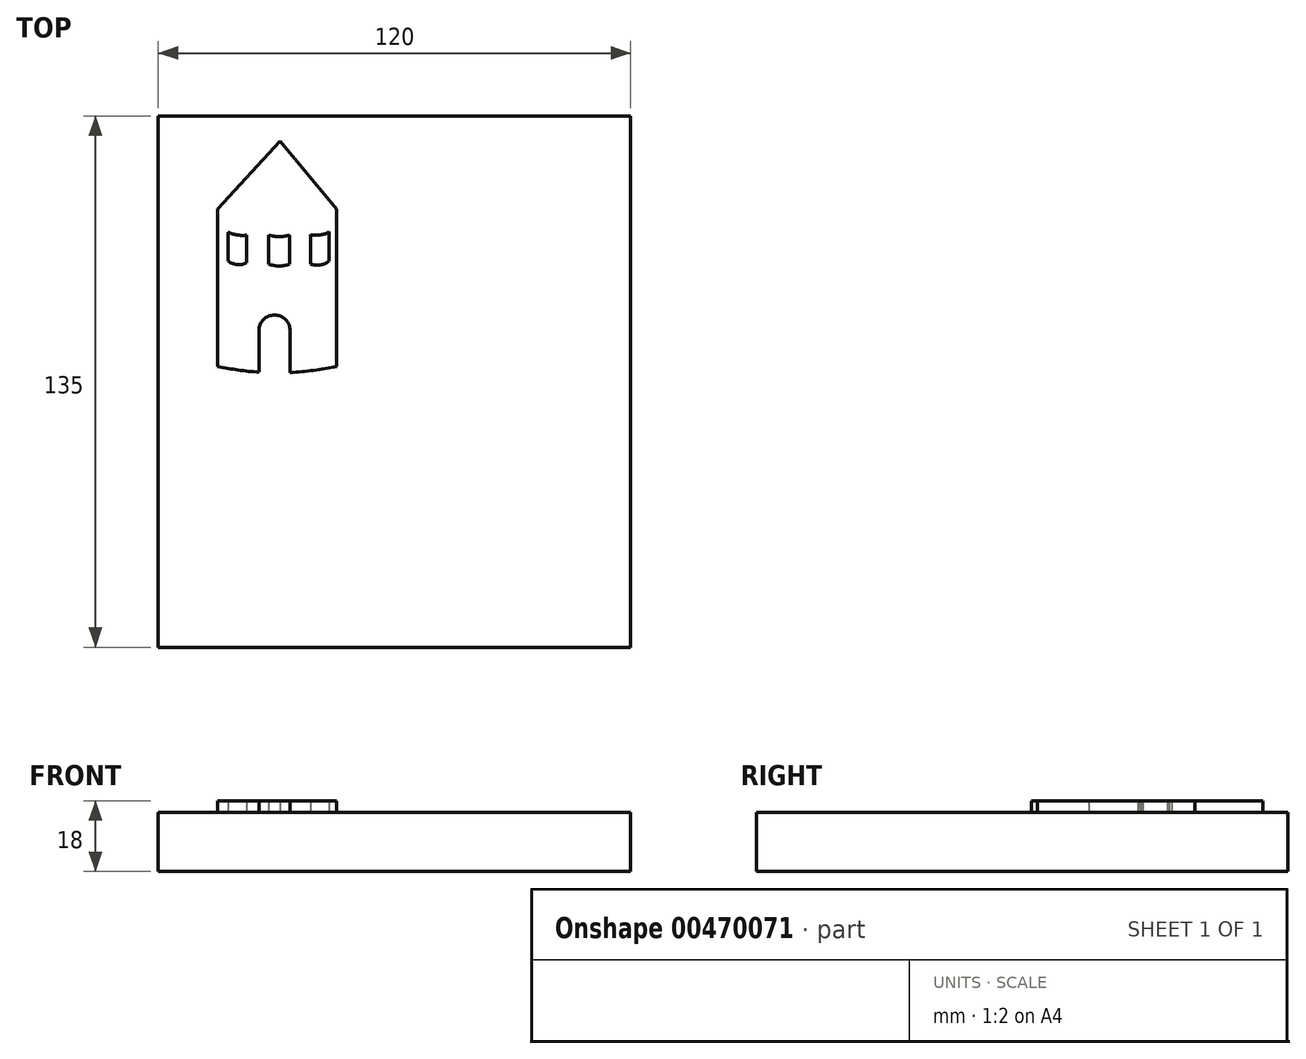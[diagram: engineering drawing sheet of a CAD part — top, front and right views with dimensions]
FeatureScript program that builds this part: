
annotation { "Feature Type Name" : "Feature", "Feature Type Description" : "" }
export const myFeature = defineFeature(function(context is Context, id is Id, definition is map)
    precondition{}
    {
        {
            var Q0;
            Q0=qCreatedBy(makeId("Top.planeOp"),FACE);
            var sketch = newSketch(context, id + "F0", { "sketchPlane" : qUnion([Q0])});
            skLineSegment(sketch, "E0.bottom", {"start": v(-60, 67.5) * mm, "end": v(60, 67.5) * mm});
            skLineSegment(sketch, "E0.top", {"start": v(-60, -67.5) * mm, "end": v(60, -67.5) * mm});
            skLineSegment(sketch, "E0.left", {"start": v(-60, 67.5) * mm, "end": v(-60, -67.5) * mm});
            skLineSegment(sketch, "E0.right", {"start": v(60, 67.5) * mm, "end": v(60, -67.5) * mm});
            skLineSegment(sketch, "E1", {"start": v(0, 67.5) * mm, "end": v(0, -67.5) * mm});
            skLineSegment(sketch, "E2", {"start": v(-60, 0) * mm, "end": v(60, 0) * mm});
            skLineSegment(sketch, "E3", {"start": v(5.98, 0) * mm, "end": v(29.66, 16.67) * mm});
            skSolve(sketch);
        }
        {
            var Q0;
            Q0=qSketchRegion(id+"F0",true);
            extrude(context, id + "F1", {"entities" : qUnion([Q0]), "depth" : 15 * mm});
        }
        {
            var Q0;
            {var subQ0=sQuery(id+"FyY21JB0s52Xvrf_1.wireOp",EDGE,"6LrTpBzl-KKAl-sDH0-PqWo-fiawwx9MfpRS");var subQ1=sQuery(id+"FyY21JB0s52Xvrf_1.wireOp",EDGE,"NrsZPt4N-Vedz-9VmN-LSZM-oJ0Oy2GTrZ6f");var subQ2=sQuery(id+"FyY21JB0s52Xvrf_1.wireOp",EDGE,"JmrGDJSe-LhiU-It9q-4cpF-6pez8Z5ADK2k");var subQ3=sQuery(id+"FyY21JB0s52Xvrf_1.wireOp",EDGE,"p0xRbvKH-dekm-qPTF-DoDm-t7GbT7wWgNVb");var subQ4=sQuery(id+"FyY21JB0s52Xvrf_1.wireOp",EDGE,"IjfTprtH-9OIw-FD3T-2Qh6-RlgL8ypDQVEx");var subQ5=sQuery(id+"FyY21JB0s52Xvrf_1.wireOp",EDGE,"o8DS8cuc-gm76-85K5-4nsE-IXK1VJtkjL9r");var subQ6=sQuery(id+"FyY21JB0s52Xvrf_1.wireOp",EDGE,"92pc5fUx-q9TN-VGGk-gwWs-JiThbNvNTNQB");var subQ7=sQuery(id+"FyY21JB0s52Xvrf_1.wireOp",EDGE,"6lok5BAO-dHQu-vOBz-bC2M-S91JDKbYCsXp");var subQ8=sQuery(id+"FyY21JB0s52Xvrf_1.wireOp",EDGE,"7nWwMa72-FhBO-tlJ7-CrnK-zSBXYpOfk1De");var subQ9=sQuery(id+"FyY21JB0s52Xvrf_1.wireOp",EDGE,"ADVGrOJx-O9Fn-WnX1-zTye-t94e958CizH2");var subQ10=sQuery(id+"F0.wireOp",EDGE,"E0.right");var subQ11=makeQuery(id+"F1.opExtrude","CAP_EDGE",EDGE,{"disambiguationData":[OSD([subQ10])],"isStart":false});var subQ12=sQuery(id+"F0.wireOp",EDGE,"E0.top");var subQ13=sQuery(id+"FyY21JB0s52Xvrf_1.wireOp",EDGE,"LoyQrscX-0LeV-IIsL-eEB7-oCOaBXq9Oc8g");var subQ14=sQuery(id+"F0.wireOp",EDGE,"E0.left");var subQ15=sQuery(id+"F0.wireOp",EDGE,"E0.bottom");var subQ16=makeQuery(id+"F1.opExtrude","CAP_FACE",FACE,{"disambiguationData":[OSD([subQ15,subQ12,subQ14,subQ10])],"isStart":false});var subQ17=sQuery(id+"FyY21JB0s52Xvrf_1.wireOp",EDGE,"No4seElB-c6sU-zyMg-Z59x-oGjhqtESyrvS");var subQ18=sQuery(id+"FyY21JB0s52Xvrf_1.wireOp",EDGE,"FQ5IqI1w-eMhy-I8kz-GYUm-XJzAXVLDYOxQ");var subQ19=sQuery(id+"FyY21JB0s52Xvrf_1.wireOp",EDGE,"arORqClW-asfx-VKiJ-l18U-UA7FszeLpePg");Q0=makeQuery(id+"FIwiPj0ks3UmRnG_1.boolean.opBoolean","SPLIT",FACE,{"disambiguationData":[TD([makeQuery(id+"F1.opExtrude","SWEPT_FACE",FACE,{"disambiguationData":[OSD([subQ15])]}),subQ16,makeQuery(id+"F1.opExtrude","SWEPT_FACE",FACE,{"disambiguationData":[OSD([subQ12])]}),makeQuery(id+"F1.opExtrude","SWEPT_FACE",FACE,{"disambiguationData":[OSD([subQ14])]}),makeQuery(id+"F1.opExtrude","SWEPT_FACE",FACE,{"disambiguationData":[OSD([subQ10])]}),makeQuery(id+"FIwiPj0ks3UmRnG_1.opExtrude","SWEPT_FACE",FACE,{"disambiguationData":[OSD([subQ18])]}),makeQuery(id+"FIwiPj0ks3UmRnG_1.opExtrude","SWEPT_FACE",FACE,{"disambiguationData":[OSD([subQ8])]}),makeQuery(id+"FIwiPj0ks3UmRnG_1.opExtrude","SWEPT_FACE",FACE,{"disambiguationData":[OSD([subQ9])]}),makeQuery(id+"FIwiPj0ks3UmRnG_1.opExtrude","SWEPT_FACE",FACE,{"disambiguationData":[OSD([subQ19])]}),makeQuery(id+"FIwiPj0ks3UmRnG_1.opExtrude","SWEPT_FACE",FACE,{"disambiguationData":[OSD([subQ7]),TDD([makeQuery(id+"FyY21JB0s52Xvrf_1.imprint","IMPRINT",EDGE,{"disambiguationData":[TD([[makeQuery(id+"FyY21JB0s52Xvrf_1.imprint","INTERSECT",VERTEX,{"derivedFrom":[subQ18,subQ7]}),1.0]])],"derivedFrom":subQ7})])]}),makeQuery(id+"FIwiPj0ks3UmRnG_1.opExtrude","SWEPT_FACE",FACE,{"disambiguationData":[OSD([subQ7]),TDD([makeQuery(id+"FyY21JB0s52Xvrf_1.imprint","IMPRINT",EDGE,{"disambiguationData":[TD([[makeQuery(id+"FyY21JB0s52Xvrf_1.imprint","INTERSECT",VERTEX,{"derivedFrom":[subQ8,subQ7]}),-1.0]])],"derivedFrom":subQ7})])]}),makeQuery(id+"FIwiPj0ks3UmRnG_1.opExtrude","SWEPT_FACE",FACE,{"disambiguationData":[OSD([subQ6]),TDD([makeQuery(id+"FyY21JB0s52Xvrf_1.imprint","IMPRINT",EDGE,{"disambiguationData":[TD([[makeQuery(id+"FyY21JB0s52Xvrf_1.imprint","INTERSECT",VERTEX,{"derivedFrom":[subQ6,subQ1]}),1.0]])],"derivedFrom":subQ6})])]}),makeQuery(id+"FIwiPj0ks3UmRnG_1.opExtrude","SWEPT_FACE",FACE,{"disambiguationData":[OSD([subQ6]),TDD([makeQuery(id+"FyY21JB0s52Xvrf_1.imprint","IMPRINT",EDGE,{"disambiguationData":[TD([[makeQuery(id+"FyY21JB0s52Xvrf_1.imprint","INTERSECT",VERTEX,{"derivedFrom":[subQ6,subQ3]}),-1.0]])],"derivedFrom":subQ6})])]}),makeQuery(id+"FIwiPj0ks3UmRnG_1.opExtrude","SWEPT_FACE",FACE,{"disambiguationData":[OSD([subQ5])]}),makeQuery(id+"FIwiPj0ks3UmRnG_1.opExtrude","SWEPT_FACE",FACE,{"disambiguationData":[OSD([subQ4])]}),makeQuery(id+"FIwiPj0ks3UmRnG_1.opExtrude","SWEPT_FACE",FACE,{"disambiguationData":[OSD([subQ3])]}),makeQuery(id+"FIwiPj0ks3UmRnG_1.opExtrude","SWEPT_FACE",FACE,{"disambiguationData":[OSD([subQ2])]}),makeQuery(id+"FIwiPj0ks3UmRnG_1.opExtrude","SWEPT_FACE",FACE,{"disambiguationData":[OSD([subQ1])]}),makeQuery(id+"FIwiPj0ks3UmRnG_1.opExtrude","SWEPT_FACE",FACE,{"disambiguationData":[OSD([subQ17])]}),makeQuery(id+"FIwiPj0ks3UmRnG_1.opExtrude","SWEPT_FACE",FACE,{"disambiguationData":[OSD([subQ0])]}),makeQuery(id+"FIwiPj0ks3UmRnG_1.opExtrude","SWEPT_FACE",FACE,{"disambiguationData":[OSD([subQ13])]}),makeQuery(id+"FIwiPj0ks3UmRnG_1.opExtrude","SWEPT_FACE",FACE,{"disambiguationData":[OSD([subQ10]),TDD([makeQuery(id+"FyY21JB0s52Xvrf_1.imprint","IMPRINT",EDGE,{"disambiguationData":[TD([[makeQuery(id+"FyY21JB0s52Xvrf_1.imprint","INTERSECT",VERTEX,{"derivedFrom":[subQ11,subQ4]}),1.0]])],"derivedFrom":subQ11})])]}),makeQuery(id+"FIwiPj0ks3UmRnG_1.opExtrude","SWEPT_FACE",FACE,{"disambiguationData":[OSD([subQ10]),TDD([makeQuery(id+"FyY21JB0s52Xvrf_1.imprint","IMPRINT",EDGE,{"disambiguationData":[TD([[makeQuery(id+"FyY21JB0s52Xvrf_1.imprint","INTERSECT",VERTEX,{"derivedFrom":[subQ11,subQ17]}),1.0]])],"derivedFrom":subQ11})])]})])],"derivedFrom":subQ16});}
            var sketch = newSketch(context, id + "F2", { "sketchPlane" : qUnion([Q0])});
            skLineSegment(sketch, "E4", {"start": v(-60, 0) * mm, "end": v(0, 0) * mm});
            skLineSegment(sketch, "E5", {"start": v(0, 0) * mm, "end": v(0, 67.5) * mm});
            skLineSegment(sketch, "E6", {"start": v(-44.92, 3.85) * mm, "end": v(-44.92, 43.85) * mm});
            skLineSegment(sketch, "E7", {"start": v(-14.68, 3.85) * mm, "end": v(-14.68, 43.85) * mm});
            skLineSegment(sketch, "E8", {"start": v(-44.92, 43.85) * mm, "end": v(-29.05, 61.11) * mm});
            skLineSegment(sketch, "E9", {"start": v(-29.05, 61.11) * mm, "end": v(-14.68, 43.85) * mm});
            skArc(sketch, "E10", {"start": v(-44.92, 43.85) * mm, "mid": v(-29.8, 42.25) * mm, "end": v(-14.68, 43.85) * mm});
            skArc(sketch, "E11", {"start": v(-44.92, 3.85) * mm, "mid": v(-29.8, 2.25) * mm, "end": v(-14.68, 3.85) * mm});
            skLineSegment(sketch, "E12", {"start": v(-34.44, 2.4) * mm, "end": v(-34.44, 12.95) * mm});
            skLineSegment(sketch, "E13", {"start": v(-26.52, 2.32) * mm, "end": v(-26.52, 12.95) * mm});
            skArc(sketch, "E14", {"start": v(-26.52, 12.95) * mm, "mid": v(-30.48, 16.9) * mm, "end": v(-34.44, 12.95) * mm});
            skLineSegment(sketch, "E15", {"start": v(-34.44, 2.4) * mm, "end": v(-31.8, 4.1) * mm});
            skLineSegment(sketch, "E16", {"start": v(-31.8, 4.1) * mm, "end": v(-31.8, 14.44) * mm});
            skArc(sketch, "E17", {"start": v(-30.48, 16.9) * mm, "mid": v(-31.46, 15.84) * mm, "end": v(-31.8, 14.44) * mm});
            skArc(sketch, "E18", {"start": v(-31.8, 4.1) * mm, "mid": v(-29.17, 3.86) * mm, "end": v(-26.52, 4.1) * mm});
            skLineSegment(sketch, "E19", {"start": v(-42.27, 38.01) * mm, "end": v(-42.27, 30.65) * mm});
            skLineSegment(sketch, "E20", {"start": v(-37.56, 30.2) * mm, "end": v(-37.56, 37.2) * mm});
            skArc(sketch, "E21", {"start": v(-42.27, 38.01) * mm, "mid": v(-39.98, 37.24) * mm, "end": v(-37.56, 37.2) * mm});
            skArc(sketch, "E22", {"start": v(-42.27, 30.65) * mm, "mid": v(-39.98, 29.73) * mm, "end": v(-37.56, 30.2) * mm});
            skLineSegment(sketch, "E23", {"start": v(-42.27, 30.65) * mm, "end": v(-40.62, 31.44) * mm});
            skLineSegment(sketch, "E24", {"start": v(-40.62, 31.44) * mm, "end": v(-40.62, 37.38) * mm});
            skArc(sketch, "E25", {"start": v(-40.62, 31.44) * mm, "mid": v(-39.1, 31.14) * mm, "end": v(-37.56, 31.44) * mm});
            skLineSegment(sketch, "E26", {"start": v(-31.97, 37.24) * mm, "end": v(-31.97, 29.9) * mm});
            skLineSegment(sketch, "E27", {"start": v(-26.6, 37.24) * mm, "end": v(-26.6, 29.9) * mm});
            skArc(sketch, "E28", {"start": v(-31.97, 29.9) * mm, "mid": v(-29.28, 29.34) * mm, "end": v(-26.6, 29.9) * mm});
            skArc(sketch, "E29", {"start": v(-31.97, 37.24) * mm, "mid": v(-29.28, 36.81) * mm, "end": v(-26.6, 37.24) * mm});
            skLineSegment(sketch, "E30", {"start": v(-31.97, 29.9) * mm, "end": v(-31.1, 30.76) * mm});
            skLineSegment(sketch, "E31", {"start": v(-31.1, 30.76) * mm, "end": v(-31.1, 37) * mm});
            skArc(sketch, "E32", {"start": v(-31.1, 30.76) * mm, "mid": v(-28.84, 30.28) * mm, "end": v(-26.6, 30.76) * mm});
            skLineSegment(sketch, "E33", {"start": v(-16.58, 38.06) * mm, "end": v(-16.58, 30.66) * mm});
            skLineSegment(sketch, "E34", {"start": v(-21.32, 37.33) * mm, "end": v(-21.32, 29.89) * mm});
            skArc(sketch, "E35", {"start": v(-21.32, 37.33) * mm, "mid": v(-18.88, 37.24) * mm, "end": v(-16.58, 38.06) * mm});
            skArc(sketch, "E36", {"start": v(-21.32, 29.89) * mm, "mid": v(-18.85, 29.65) * mm, "end": v(-16.58, 30.66) * mm});
            skLineSegment(sketch, "E37", {"start": v(-16.58, 30.66) * mm, "end": v(-17.93, 31.14) * mm});
            skLineSegment(sketch, "E38", {"start": v(-17.93, 31.14) * mm, "end": v(-17.93, 37.46) * mm});
            skSolve(sketch);
        }
        {
            var Q0;
            {var subQ18=sQuery(id+"F2.wireOp",EDGE,"E6");Q0=makeQuery(id+"F2.imprint","IMPRINT",FACE,{"disambiguationData":[TD([[makeQuery(id+"F2.imprint","IMPRINT",EDGE,{"derivedFrom":subQ18}),-1.0]])]});}
            var Q1;
            Q1=makeQuery(id+"F2.imprint","IMPRINT",FACE,{"disambiguationData":[TD([[makeQuery(id+"F2.imprint","IMPRINT",EDGE,{"derivedFrom":sQuery(id+"F2.wireOp",EDGE,"E8")}),-1.0]])]});
            extrude(context, id + "F3", {"entities" : qUnion([Q0, Q1]), "operationType" : NewBodyOperationType.ADD, "depth" : 3 * mm});
        }
    });
